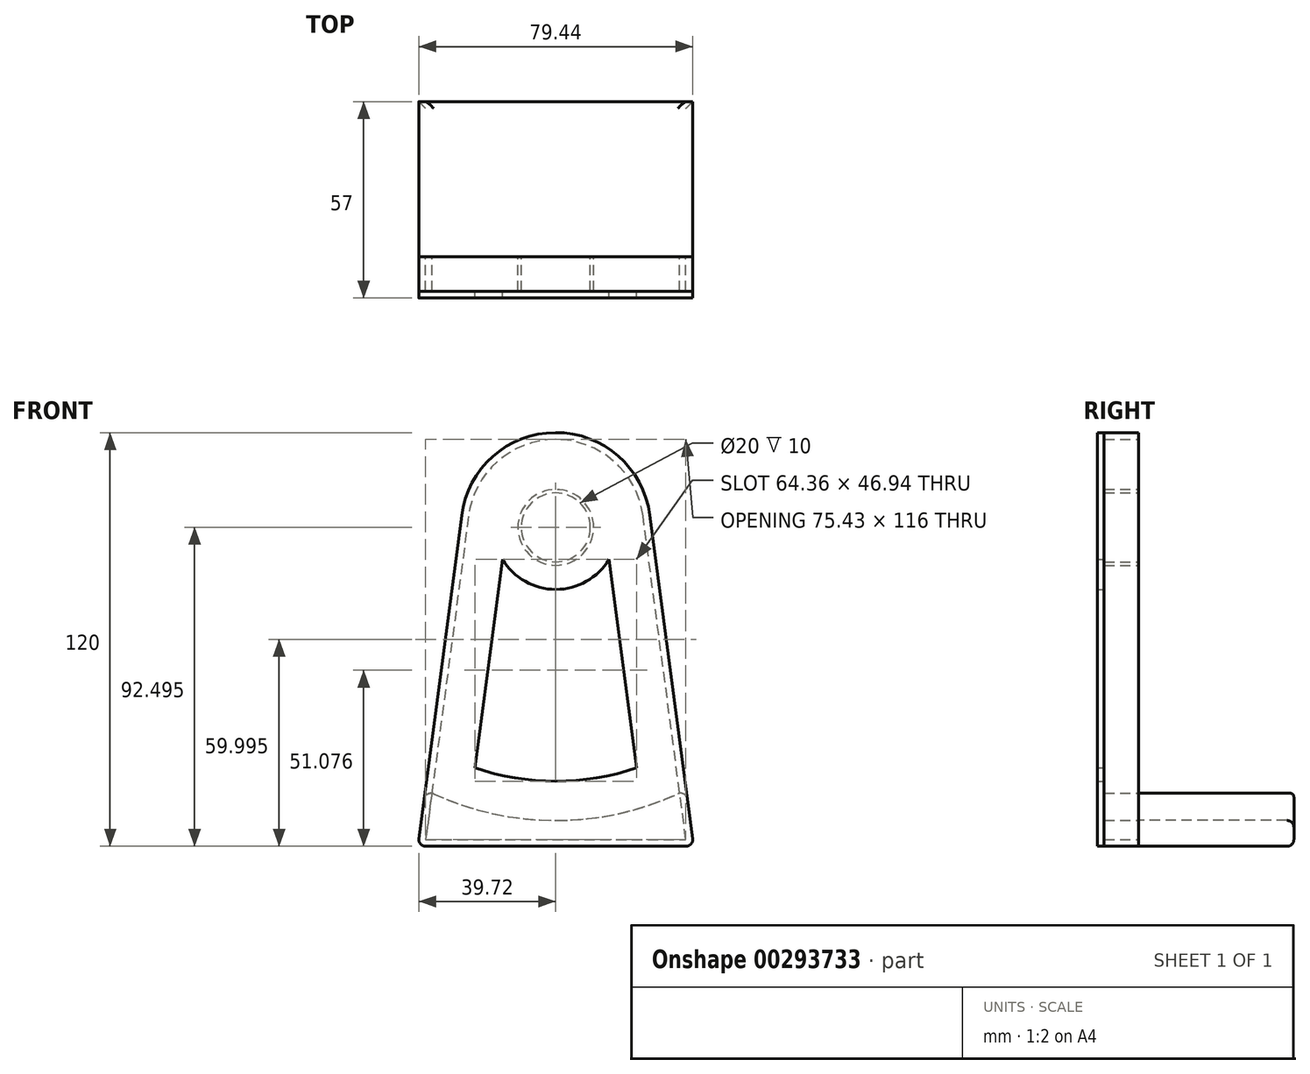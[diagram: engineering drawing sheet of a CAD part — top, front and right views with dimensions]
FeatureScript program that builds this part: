
annotation { "Feature Type Name" : "Feature", "Feature Type Description" : "" }
export const myFeature = defineFeature(function(context is Context, id is Id, definition is map)
    precondition{}
    {
        {
            var Q0;
            Q0=qCreatedBy(makeId("Front.planeOp"),FACE);
            var sketch = newSketch(context, id + "F0", { "sketchPlane" : qUnion([Q0])});
            skArc(sketch, "E0", {"start": v(27.26, 48.15) * mm, "mid": v(-0.12, 72.04) * mm, "end": v(-27.3, 47.91) * mm});
            skLineSegment(sketch, "E1", {"start": v(-27.3, 47.91) * mm, "end": v(-40, -47.96) * mm});
            skLineSegment(sketch, "E2", {"start": v(-40, -47.96) * mm, "end": v(40, -47.96) * mm});
            skLineSegment(sketch, "E3", {"start": v(40, -47.96) * mm, "end": v(27.26, 48.15) * mm});
            skCircle(sketch, "E4", {"center": v(0, 44.54) * mm, "radius": 10 * mm});
            skCircle(sketch, "E5", {"center": v(0, 44.54) * mm, "radius": 11 * mm});
            skLineSegment(sketch, "E6.0", {"start": v(-25.3, 47.66) * mm, "end": v(-37.72, -45.96) * mm});
            skArc(sketch, "E6.1", {"start": v(25.28, 47.89) * mm, "mid": v(-0.11, 70.04) * mm, "end": v(-25.3, 47.66) * mm});
            skLineSegment(sketch, "E6.2", {"start": v(37.72, -45.96) * mm, "end": v(25.28, 47.89) * mm});
            skLineSegment(sketch, "E6.3", {"start": v(-37.72, -45.96) * mm, "end": v(37.72, -45.96) * mm});
            skSolve(sketch);
        }
        {
            var Q0;
            Q0=makeQuery(id+"F0.imprint","IMPRINT",FACE,{"disambiguationData":[TD([[makeQuery(id+"F0.imprint","IMPRINT",EDGE,{"derivedFrom":sQuery(id+"F0.wireOp",EDGE,"E0")}),1.0]])]});
            var Q1;
            Q1=makeQuery(id+"F0.imprint","IMPRINT",FACE,{"disambiguationData":[TD([[makeQuery(id+"F0.imprint","IMPRINT",EDGE,{"derivedFrom":sQuery(id+"F0.wireOp",EDGE,"E4")}),-1.0]])]});
            extrude(context, id + "F1", {"entities" : qUnion([Q0, Q1]), "depth" : 10 * mm});
        }
        {
            var Q0;
            Q0=makeQuery(id+"F1.opExtrude","CAP_FACE",FACE,{"disambiguationData":[OSD([sQuery(id+"F0.wireOp",EDGE,"E0"),sQuery(id+"F0.wireOp",EDGE,"E1"),sQuery(id+"F0.wireOp",EDGE,"E2"),sQuery(id+"F0.wireOp",EDGE,"E3"),sQuery(id+"F0.wireOp",EDGE,"E6.0"),sQuery(id+"F0.wireOp",EDGE,"E6.1"),sQuery(id+"F0.wireOp",EDGE,"E6.2"),sQuery(id+"F0.wireOp",EDGE,"E6.3")])],"isStart":false});
            var sketch = newSketch(context, id + "F2", { "sketchPlane" : qUnion([Q0])});
            skArc(sketch, "E7.0", {"start": v(27.26, 48.15) * mm, "mid": v(-0.12, 72.04) * mm, "end": v(-27.3, 47.91) * mm});
            skLineSegment(sketch, "E7.1", {"start": v(40, -47.96) * mm, "end": v(27.26, 48.15) * mm});
            skLineSegment(sketch, "E7.2", {"start": v(-40, -47.96) * mm, "end": v(40, -47.96) * mm});
            skLineSegment(sketch, "E7.3", {"start": v(-27.3, 47.91) * mm, "end": v(-40, -47.96) * mm});
            skSolve(sketch);
        }
        {
            var Q0;
            Q0 = qSketchRegion(id + "F2", true);
            extrude(context, id + "F3", {"entities" : qUnion([Q0]), "depth" : 2 * mm});
        }
        {
            var Q0;
            Q0=makeQuery(id+"F1.opExtrude","CAP_FACE",FACE,{"disambiguationData":[OSD([sQuery(id+"F0.wireOp",EDGE,"E0"),sQuery(id+"F0.wireOp",EDGE,"E1"),sQuery(id+"F0.wireOp",EDGE,"E2"),sQuery(id+"F0.wireOp",EDGE,"E3"),sQuery(id+"F0.wireOp",EDGE,"E6.0"),sQuery(id+"F0.wireOp",EDGE,"E6.1"),sQuery(id+"F0.wireOp",EDGE,"E6.2"),sQuery(id+"F0.wireOp",EDGE,"E6.3")])],"isStart":true});
            var sketch = newSketch(context, id + "F4", { "sketchPlane" : qUnion([Q0])});
            skLineSegment(sketch, "E8.0", {"start": v(-40, -47.96) * mm, "end": v(-37.83, -31.58) * mm});
            skLineSegment(sketch, "E8.1", {"start": v(40, -47.96) * mm, "end": v(-40, -47.96) * mm});
            skLineSegment(sketch, "E8.2", {"start": v(37.83, -31.58) * mm, "end": v(40, -47.96) * mm});
            skArc(sketch, "E9", {"start": v(-37.83, -31.58) * mm, "mid": v(0, -40.46) * mm, "end": v(37.83, -31.58) * mm});
            skPoint(sketch, "E10.orphan", {"position": v(-27.26, 48.15) * mm});
            skPoint(sketch, "E11.orphan", {"position": v(27.3, 47.91) * mm});
            skSolve(sketch);
        }
        {
            var Q0;
            {var subQ5=makeQuery(id+"F1.opExtrude","CAP_EDGE",EDGE,{"disambiguationData":[OSD([sQuery(id+"F0.wireOp",EDGE,"E6.3")])],"isStart":true});Q0=makeQuery(id+"F4.imprint","IMPRINT",FACE,{"disambiguationData":[TD([[makeQuery(id+"F4.imprint","IMPRINT",EDGE,{"derivedFrom":subQ5}),-1.0]])]});}
            extrude(context, id + "F5", {"entities" : qUnion([Q0]), "endBound" : BoundingType.UP_TO_NEXT, "oppositeDirection" : true, "depth" : 25 * mm});
        }
        {
            var Q0;
            Q0=makeQuery(id+"F5.opExtrude","CAP_FACE",FACE,{"disambiguationData":[OSD([sQuery(id+"F0.wireOp",EDGE,"E6.0"),sQuery(id+"F0.wireOp",EDGE,"E6.2"),sQuery(id+"F0.wireOp",EDGE,"E6.3"),sQuery(id+"F4.wireOp",EDGE,"E9")])],"isStart":true});
            var sketch = newSketch(context, id + "F6", { "sketchPlane" : qUnion([Q0])});
            skLineSegment(sketch, "E12.0", {"start": v(-40, -47.96) * mm, "end": v(-37.83, -31.58) * mm});
            skLineSegment(sketch, "E12.1", {"start": v(40, -47.96) * mm, "end": v(-40, -47.96) * mm});
            skLineSegment(sketch, "E12.2", {"start": v(37.83, -31.58) * mm, "end": v(40, -47.96) * mm});
            skArc(sketch, "E12.3", {"start": v(-37.83, -31.58) * mm, "mid": v(0, -40.46) * mm, "end": v(37.83, -31.58) * mm});
            skPoint(sketch, "E12.4", {"position": v(-27.26, 48.15) * mm});
            skPoint(sketch, "E12.5", {"position": v(27.3, 47.91) * mm});
            skSolve(sketch);
        }
        {
            var Q0;
            Q0 = qSketchRegion(id + "F6", true);
            extrude(context, id + "F7", {"entities" : qUnion([Q0]), "depth" : 45 * mm});
        }
        {
            var Q0;
            Q0=makeQuery(id+"F7.opExtrude","SWEPT_EDGE",EDGE,{"disambiguationData":[OSD([sQuery(id+"F6.wireOp",EDGE,"E12.1"),sQuery(id+"F6.wireOp",EDGE,"E12.2")])]});
            var Q1;
            Q1=makeQuery(id+"F1.opExtrude","SWEPT_EDGE",EDGE,{"disambiguationData":[OSD([sQuery(id+"F0.wireOp",EDGE,"E1"),sQuery(id+"F0.wireOp",EDGE,"E2")])]});
            var Q2;
            Q2=makeQuery(id+"F3.opExtrude","SWEPT_EDGE",EDGE,{"disambiguationData":[OSD([sQuery(id+"F2.wireOp",EDGE,"E7.2"),sQuery(id+"F2.wireOp",EDGE,"E7.3")])]});
            var Q3;
            Q3=makeQuery(id+"F7.opExtrude","CAP_EDGE",EDGE,{"disambiguationData":[OSD([sQuery(id+"F6.wireOp",EDGE,"E12.1")])],"isStart":false});
            var Q4;
            Q4=makeQuery(id+"F7.opExtrude","SWEPT_EDGE",EDGE,{"disambiguationData":[OSD([sQuery(id+"F6.wireOp",EDGE,"E12.0"),sQuery(id+"F6.wireOp",EDGE,"E12.1")])]});
            var Q5;
            Q5=makeQuery(id+"F1.opExtrude","SWEPT_EDGE",EDGE,{"disambiguationData":[OSD([sQuery(id+"F0.wireOp",EDGE,"E2"),sQuery(id+"F0.wireOp",EDGE,"E3")])]});
            var Q6;
            Q6=makeQuery(id+"F3.opExtrude","SWEPT_EDGE",EDGE,{"disambiguationData":[OSD([sQuery(id+"F2.wireOp",EDGE,"E7.1"),sQuery(id+"F2.wireOp",EDGE,"E7.2")])]});
            fillet(context, id + "F8", {"entities" : qUnion([Q0, Q1, Q2, Q3, Q4, Q5, Q6]), "radius" : 2 * mm, "tangentPropagation" : true, "allowEdgeOverflow" : false});
        }
        {
            var Q0;
            Q0=makeQuery(id+"F7.opExtrude","CAP_EDGE",EDGE,{"disambiguationData":[OSD([sQuery(id+"F6.wireOp",EDGE,"E12.3")])],"isStart":false});
            var Q1;
            Q1=makeQuery(id+"F7.opExtrude","SWEPT_EDGE",EDGE,{"disambiguationData":[OSD([sQuery(id+"F6.wireOp",EDGE,"E12.0"),sQuery(id+"F6.wireOp",EDGE,"E12.3")])]});
            var Q2;
            Q2=makeQuery(id+"F7.opExtrude","SWEPT_EDGE",EDGE,{"disambiguationData":[OSD([sQuery(id+"F6.wireOp",EDGE,"E12.2"),sQuery(id+"F6.wireOp",EDGE,"E12.3")])]});
            fillet(context, id + "F9", {"entities" : qUnion([Q0, Q1, Q2]), "radius" : 2 * mm, "tangentPropagation" : true, "allowEdgeOverflow" : false});
        }
        {
            var Q0;
            Q0=makeQuery(id+"F3.opExtrude","CAP_FACE",FACE,{"disambiguationData":[OSD([sQuery(id+"F2.wireOp",EDGE,"E7.0"),sQuery(id+"F2.wireOp",EDGE,"E7.1"),sQuery(id+"F2.wireOp",EDGE,"E7.2"),sQuery(id+"F2.wireOp",EDGE,"E7.3")])],"isStart":true});
            var sketch = newSketch(context, id + "F10", { "sketchPlane" : qUnion([Q0])});
            skLineSegment(sketch, "E13.0", {"start": v(-35.93, -32.5) * mm, "end": v(-25.28, 47.89) * mm});
            skLineSegment(sketch, "E13.2", {"start": v(25.3, 47.66) * mm, "end": v(35.93, -32.5) * mm});
            skPoint(sketch, "E13.3", {"position": v(0, -40.46) * mm});
            skArc(sketch, "E14.0", {"start": v(-35.93, -32.5) * mm, "mid": v(0, -40.46) * mm, "end": v(35.93, -32.5) * mm});
            skLineSegment(sketch, "E15.0", {"start": v(-23.47, -25.22) * mm, "end": v(-15.45, 35.3) * mm});
            skArc(sketch, "E15.1", {"start": v(-23.47, -25.22) * mm, "mid": v(0, -29.06) * mm, "end": v(23.47, -25.22) * mm});
            skLineSegment(sketch, "E15.2", {"start": v(15.45, 35.3) * mm, "end": v(23.47, -25.22) * mm});
            skArc(sketch, "E16", {"start": v(-15.45, 35.3) * mm, "mid": v(0, 26.54) * mm, "end": v(15.45, 35.3) * mm});
            skSolve(sketch);
        }
        {
            var Q0;
            Q0=makeQuery(id+"F10.imprint","IMPRINT",FACE,{"disambiguationData":[TD([[makeQuery(id+"F10.imprint","IMPRINT",EDGE,{"derivedFrom":sQuery(id+"F10.wireOp",EDGE,"E15.0")}),-1.0]])]});
            extrude(context, id + "F11", {"entities" : qUnion([Q0]), "operationType" : NewBodyOperationType.REMOVE, "oppositeDirection" : true, "depth" : 6 * mm});
        }
    });
